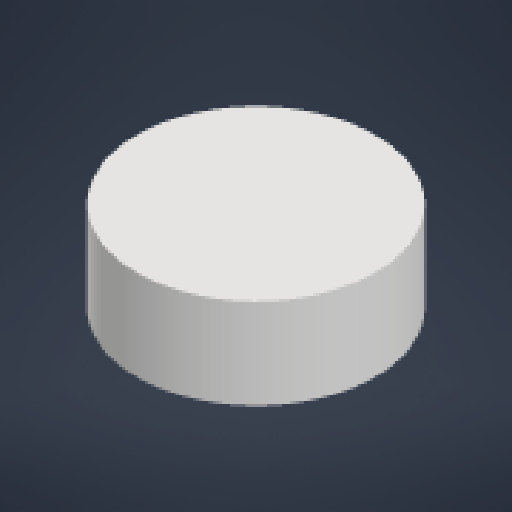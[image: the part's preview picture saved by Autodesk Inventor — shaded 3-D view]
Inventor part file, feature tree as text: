
AUTODESK INVENTOR PART (.ipt)
format: ipt  version: 2024.2 (Build 282272000, 272)  size: 343,040 bytes
history: native  units: in
note: dims shown in document units (in); Inventor stores cm internally (conversion verified against a paired STEP export)
features: revolve x1, sketch x1
ambient origin geometry x8: Origin, YZ Plane, XZ Plane, XY Plane, X Axis, Y Axis, Z Axis, Center Point
bodies: Body1 (feature_tree)
feature tree (2):
  revolve  "Revolution1"  [1 undecoded]
  sketch  "Sketch4"  dims[d12=1.024in d13=1.3173in d14=0.072in d16=6.6929in d18=0.06in d19=0.3937in d21=1.0in d25=0.028in d26=0.0017in d27=0.004in d28=0.0in d29=360.0deg d3=0.5in d4=0.0344in d5=0.5in d6=0.0344in d30=0.0344in d31=0.0344in]
note: 1 required parameter value undecoded (feature->parameter linkage not recoverable at this tier; creation-order binding heuristic only, values carry confidence <= 0.55)
